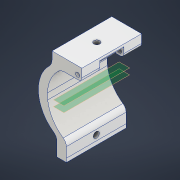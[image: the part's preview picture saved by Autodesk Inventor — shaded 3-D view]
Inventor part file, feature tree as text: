
AUTODESK INVENTOR PART (.ipt)
format: ipt  version: 2021 (Build 250183000, 183)  size: 209,920 bytes
history: native  units: in
note: dims shown in document units (in); Inventor stores cm internally (conversion verified against a paired STEP export)
features: fillet x5, sketch x5, extrude x4, hole x2, plane x2, split x2
ambient origin geometry x8: Origin, YZ Plane, XZ Plane, XY Plane, X Axis, Y Axis, Z Axis, Center Point
bodies: Solid1 (feature_tree)
feature tree (20):
  extrude  "Extrusion1"  Depth=3.937in TaperAngle=0.0deg
  extrude  "Extrusion6"  Depth=1.9685in
  extrude  "Extrusion8"  Depth=2.3622in
  extrude  "Extrusion9"  Depth=0.2756in
  hole  "Hole4"  [1 undecoded]
  fillet  "Fillet1"  Radius=3.937in
  fillet  "Fillet2"  Radius=0.5118in
  fillet  "Fillet3"  Radius=0.5906in
  fillet  "Fillet4"  Radius=0.3937in
  fillet  "Fillet5"  Radius=0.2362in
  plane  "Work Plane2"
  plane  "Work Plane3"
  split  "Split3"
  split  "Split4"
  hole  "Hole5"  [1 undecoded]
  sketch  "Sketch2"  dims[d1=1.9685in d2=3.937in d3=0.0in]
  sketch  "Sketch12"  dims[d56=3.937in d57=1.9685in]
  sketch  "Sketch18"  dims[d58=2.3622in d59=1.1811in]
  sketch  "Sketch19"  dims[d62=3.937in d63=0.0in d82=0.2756in]
  sketch  "Sketch20"  dims[d83=0.2756in d84=0.2756in d85=3.937in d86=0.0in d89=0.5118in d90=0.0in d91=0.5906in d92=0.3937in d93=0.3937in d94=0.2362in d95=0.3937in d96=0.1181in d97=90.0deg d98=0.315in d99=0.8108in d102=0.2362in d103=2.3622in d104=0.5512in d105=0.7874in d106=0.7874in d108=0.6299in d109=0.6299in d110=0.6299in d111=0.4724in d112=0.5906in d113=0.0787in d114=-3.3465in d115=-2.9528in d116=1.9685in d117=3.937in d118=1.9685in d119=0.9843in d120=0.3937in d121=0.2362in d122=0.1575in d123=0.0787in d124=90.0deg d125=0.315in d126=0.8108in d64=0.0197in d65=0.0344in d66=0.0197in d67=0.0344in d75=0.0394in d76=0.0394in d77=0.0394in d78=0.0059in d79=0.0098in d80=0.0148in d81=0.5635in]
note: 2 required parameter values undecoded (feature->parameter linkage not recoverable at this tier; creation-order binding heuristic only, values carry confidence <= 0.55)
